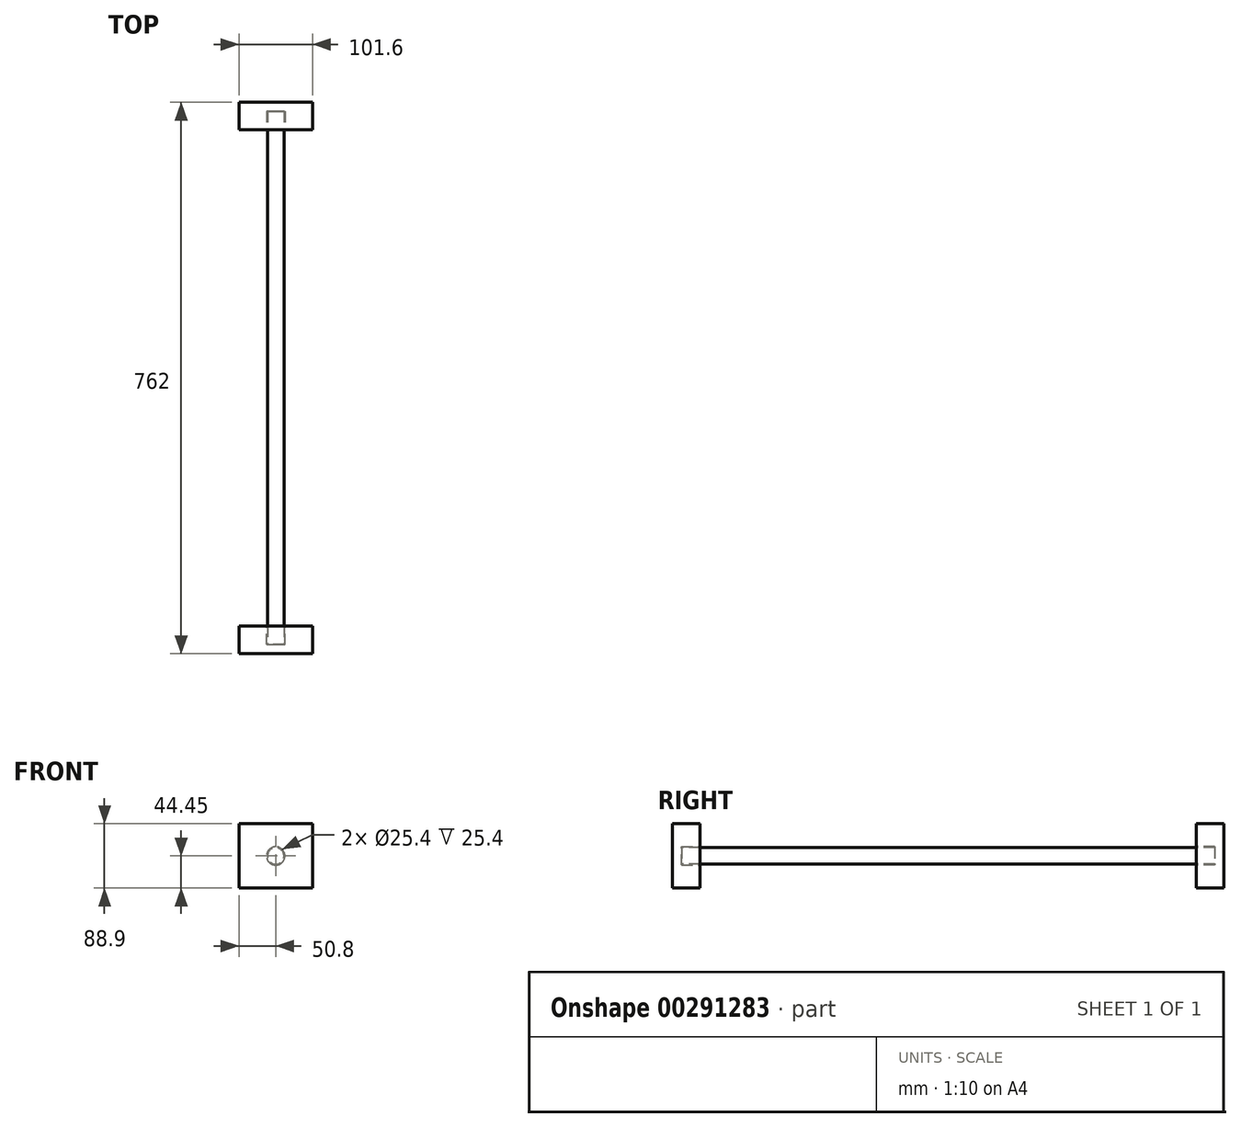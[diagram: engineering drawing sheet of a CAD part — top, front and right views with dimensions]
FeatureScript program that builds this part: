
annotation { "Feature Type Name" : "Feature", "Feature Type Description" : "" }
export const myFeature = defineFeature(function(context is Context, id is Id, definition is map)
    precondition{}
    {
        {
            var Q0;
            Q0=qCreatedBy(makeId("Right.planeOp"),FACE);
            var sketch = newSketch(context, id + "F0", { "sketchPlane" : qUnion([Q0])});
            skLineSegment(sketch, "E0", {"start": v(0, 0) * mm, "end": v(-368.3, 0) * mm});
            skLineSegment(sketch, "E1", {"start": v(0, 0) * mm, "end": v(368.3, 0) * mm});
            skLineSegment(sketch, "E2", {"start": v(-342.9, 0) * mm, "end": v(-342.9, 44.45) * mm});
            skLineSegment(sketch, "E3", {"start": v(-342.9, 44.45) * mm, "end": v(-381, 44.45) * mm});
            skLineSegment(sketch, "E4", {"start": v(-381, 44.45) * mm, "end": v(-381, -44.45) * mm});
            skLineSegment(sketch, "E5", {"start": v(-381, -44.45) * mm, "end": v(-342.9, -44.45) * mm});
            skLineSegment(sketch, "E6", {"start": v(-342.9, -44.45) * mm, "end": v(-342.9, 0) * mm});
            skLineSegment(sketch, "E7", {"start": v(0, 0) * mm, "end": v(0, 80.33) * mm});
            skLineSegment(sketch, "E8.MirrorCS", {"start": v(342.9, 0) * mm, "end": v(342.9, 44.45) * mm});
            skLineSegment(sketch, "E9.MirrorCS", {"start": v(381, -44.45) * mm, "end": v(342.9, -44.45) * mm});
            skLineSegment(sketch, "E10.MirrorCS", {"start": v(342.9, 44.45) * mm, "end": v(381, 44.45) * mm});
            skLineSegment(sketch, "E11.MirrorCS", {"start": v(381, 44.45) * mm, "end": v(381, -44.45) * mm});
            skLineSegment(sketch, "E12.MirrorCS", {"start": v(342.9, -44.45) * mm, "end": v(342.9, 0) * mm});
            skSolve(sketch);
        }
        {
            var Q0;
            Q0 = qSketchRegion(id + "F0", true);
            extrude(context, id + "F1", {"entities" : qUnion([Q0]), "depth" : 101.6 * mm});
        }
        {
            var Q0;
            Q0=makeQuery(id+"F1.opExtrude","SWEPT_FACE",FACE,{"disambiguationData":[OSD([sQuery(id+"F0.wireOp",EDGE,"E2"),sQuery(id+"F0.wireOp",EDGE,"E6")])]});
            var sketch = newSketch(context, id + "F2", { "sketchPlane" : qUnion([Q0])});
            skCircle(sketch, "E13", {"center": v(-50.8, 0) * mm, "radius": 12.7 * mm});
            skSolve(sketch);
        }
        {
            var Q0;
            Q0 = qSketchRegion(id + "F2", true);
            extrude(context, id + "F3", {"entities" : qUnion([Q0]), "operationType" : NewBodyOperationType.REMOVE, "depth" : 711.2 * mm});
        }
        {
            var Q0;
            Q0=makeQuery(id+"F1.opExtrude","SWEPT_FACE",FACE,{"disambiguationData":[OSD([sQuery(id+"F0.wireOp",EDGE,"E8.MirrorCS"),sQuery(id+"F0.wireOp",EDGE,"E12.MirrorCS")])]});
            var sketch = newSketch(context, id + "F4", { "sketchPlane" : qUnion([Q0])});
            skCircle(sketch, "E14", {"center": v(50.8, 0) * mm, "radius": 12.7 * mm});
            skSolve(sketch);
        }
        {
            var Q0;
            Q0 = qSketchRegion(id + "F4", true);
            extrude(context, id + "F5", {"entities" : qUnion([Q0]), "operationType" : NewBodyOperationType.REMOVE, "depth" : 711.2 * mm});
        }
        {
            var Q0;
            Q0=makeQuery(id+"F5.boolean.opBoolean","COPY",FACE,{"derivedFrom":makeQuery(id+"F5.opExtrude","CAP_FACE",FACE,{"disambiguationData":[OSD([sQuery(id+"F4.wireOp",EDGE,"E14")])],"isStart":false})});
            var sketch = newSketch(context, id + "F6", { "sketchPlane" : qUnion([Q0])});
            skCircle(sketch, "E15", {"center": v(-50.8, 0) * mm, "radius": 11.43 * mm});
            skSolve(sketch);
        }
        {
            var Q0;
            Q0 = qSketchRegion(id + "F6", true);
            extrude(context, id + "F7", {"entities" : qUnion([Q0]), "depth" : 736.6 * mm});
        }
    });
